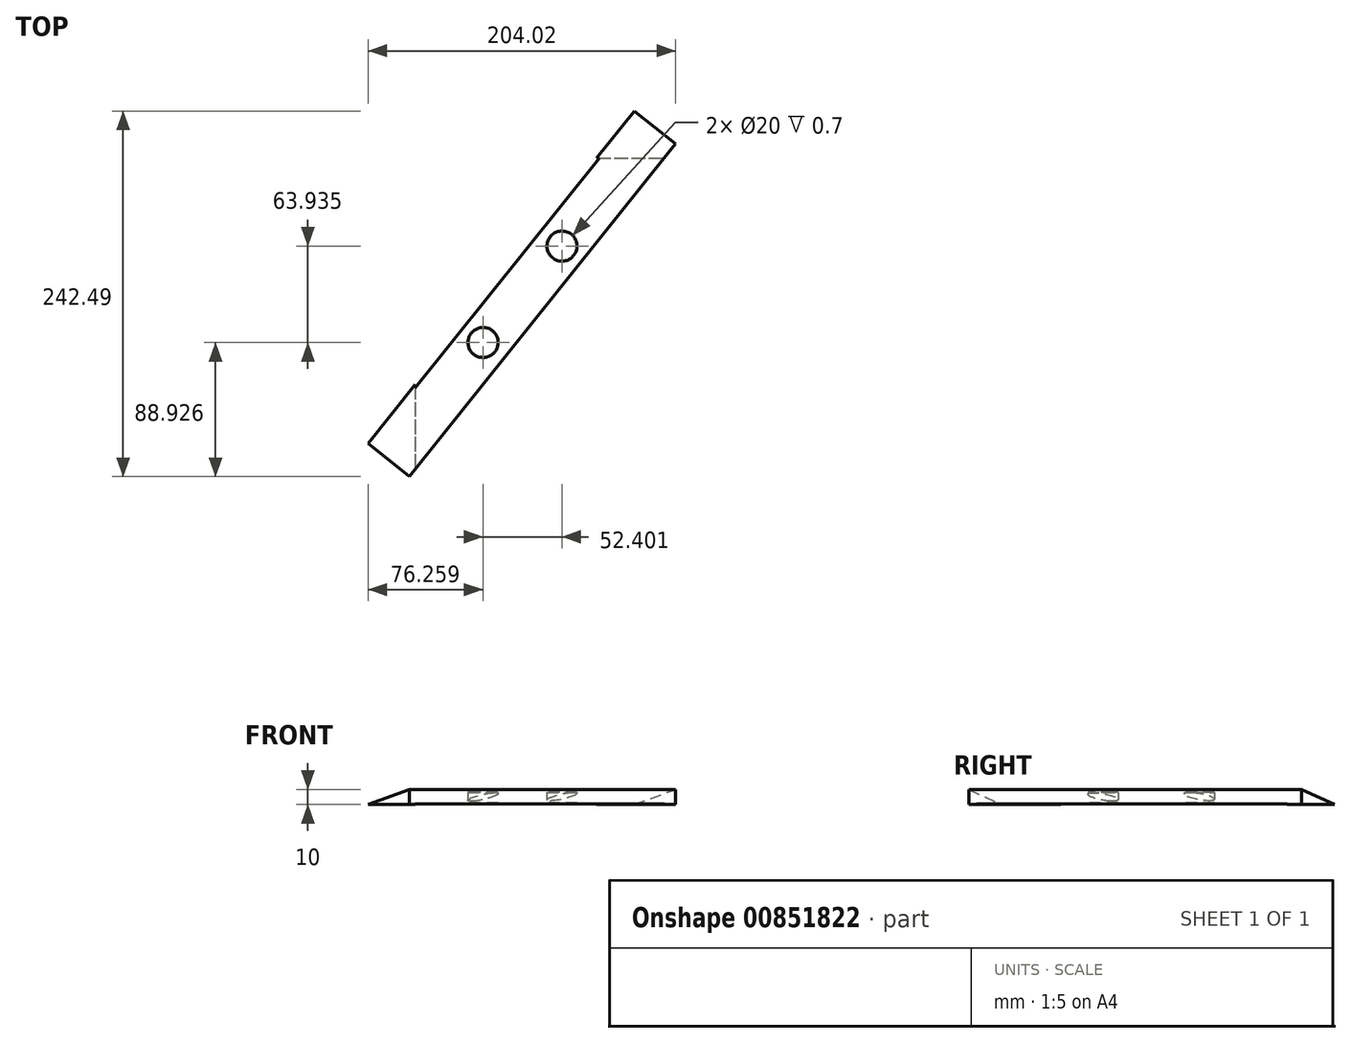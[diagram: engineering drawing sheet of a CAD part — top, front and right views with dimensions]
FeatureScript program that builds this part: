
annotation { "Feature Type Name" : "Feature", "Feature Type Description" : "" }
export const myFeature = defineFeature(function(context is Context, id is Id, definition is map)
    precondition{}
    {
        {
            var Q0;
            Q0=qCreatedBy(makeId("Top.planeOp"),FACE);
            var sketch = newSketch(context, id + "F0", { "sketchPlane" : qUnion([Q0])});
            skLineSegment(sketch, "E0.bottom", {"start": v(-264.2, 336.11) * mm, "end": v(-24.2, 336.11) * mm});
            skLineSegment(sketch, "E0.top", {"start": v(-264.2, 16.11) * mm, "end": v(-24.2, 16.11) * mm});
            skLineSegment(sketch, "E0.left", {"start": v(-264.2, 336.11) * mm, "end": v(-264.2, 16.11) * mm});
            skLineSegment(sketch, "E0.right", {"start": v(-24.2, 336.11) * mm, "end": v(-24.2, 16.11) * mm});
            skLineSegment(sketch, "E1", {"start": v(-264.2, 185.75) * mm, "end": v(-108.6, 61.11) * mm});
            skLineSegment(sketch, "E2", {"start": v(-264.2, 185.75) * mm, "end": v(-143.77, 336.11) * mm});
            skLineSegment(sketch, "E3", {"start": v(-108.6, 61.11) * mm, "end": v(-24.2, 166.48) * mm});
            skLineSegment(sketch, "E4", {"start": v(-24.2, 166.48) * mm, "end": v(-179.81, 291.11) * mm});
            skLineSegment(sketch, "E5.bottom", {"start": v(-268.15, 124.84) * mm, "end": v(-91.45, 345.45) * mm});
            skLineSegment(sketch, "E5.top", {"start": v(-295.47, 146.72) * mm, "end": v(-118.77, 367.33) * mm});
            skLineSegment(sketch, "E5.left", {"start": v(-295.47, 146.72) * mm, "end": v(-268.15, 124.84) * mm});
            skLineSegment(sketch, "E5.right", {"start": v(-118.77, 367.33) * mm, "end": v(-91.45, 345.45) * mm});
            skLineSegment(sketch, "E6.bottom", {"start": v(-257.84, 237.67) * mm, "end": v(-285.66, 202.93) * mm});
            skLineSegment(sketch, "E6.top", {"start": v(-13.84, 42.24) * mm, "end": v(-41.66, 7.5) * mm});
            skLineSegment(sketch, "E6.left", {"start": v(-285.66, 202.93) * mm, "end": v(-41.66, 7.5) * mm});
            skLineSegment(sketch, "E6.right", {"start": v(-257.84, 237.67) * mm, "end": v(-13.84, 42.24) * mm});
            skSolve(sketch);
        }
        {
            var Q0;
            {var subQ5=sQuery(id+"F0.wireOp",EDGE,"E5.right");Q0=makeQuery(id+"F0.imprint","IMPRINT",FACE,{"disambiguationData":[TD([[makeQuery(id+"F0.imprint","IMPRINT",EDGE,{"derivedFrom":subQ5}),-1.0]])]});}
            var Q1;
            {var subQ3=sQuery(id+"F0.wireOp",EDGE,"E2");var subQ5=sQuery(id+"F0.wireOp",EDGE,"E4");var subQ6=makeQuery(id+"F0.imprint","INTERSECT",VERTEX,{"derivedFrom":[subQ3,subQ5]});Q1=makeQuery(id+"F0.imprint","IMPRINT",FACE,{"disambiguationData":[TD([[makeQuery(id+"F0.imprint","IMPRINT",EDGE,{"disambiguationData":[TD([[subQ6,1.0]])],"derivedFrom":subQ5}),-1.0]])]});}
            var Q2;
            {var subQ0=sQuery(id+"F0.wireOp",EDGE,"E6.right");var subQ1=sQuery(id+"F0.wireOp",EDGE,"E2");var subQ2=makeQuery(id+"F0.imprint","INTERSECT",VERTEX,{"derivedFrom":[subQ1,subQ0]});Q2=makeQuery(id+"F0.imprint","IMPRINT",FACE,{"disambiguationData":[TD([[makeQuery(id+"F0.imprint","IMPRINT",EDGE,{"disambiguationData":[TD([[subQ2,-1.0]])],"derivedFrom":subQ1}),-1.0]])]});}
            var Q3;
            {var subQ5=sQuery(id+"F0.wireOp",EDGE,"E5.left");Q3=makeQuery(id+"F0.imprint","IMPRINT",FACE,{"disambiguationData":[TD([[makeQuery(id+"F0.imprint","IMPRINT",EDGE,{"derivedFrom":subQ5}),1.0]])]});}
            var Q4;
            {var subQ0=sQuery(id+"F0.wireOp",EDGE,"E5.bottom");var subQ1=sQuery(id+"F0.wireOp",EDGE,"E0.left");var subQ2=makeQuery(id+"F0.imprint","INTERSECT",VERTEX,{"derivedFrom":[subQ1,subQ0]});Q4=makeQuery(id+"F0.imprint","IMPRINT",FACE,{"disambiguationData":[TD([[makeQuery(id+"F0.imprint","IMPRINT",EDGE,{"disambiguationData":[TD([[subQ2,-1.0]])],"derivedFrom":subQ0}),1.0]])]});}
            var Q5;
            {var subQ1=sQuery(id+"F0.wireOp",EDGE,"E1");var subQ3=sQuery(id+"F0.wireOp",EDGE,"E5.bottom");var subQ4=makeQuery(id+"F0.imprint","INTERSECT",VERTEX,{"derivedFrom":[subQ1,subQ3]});Q5=makeQuery(id+"F0.imprint","IMPRINT",FACE,{"disambiguationData":[TD([[makeQuery(id+"F0.imprint","IMPRINT",EDGE,{"disambiguationData":[TD([[subQ4,-1.0]])],"derivedFrom":subQ3}),1.0]])]});}
            extrude(context, id + "F1", {"entities" : qUnion([Q0, Q1, Q2, Q3, Q4, Q5]), "depth" : 10 * mm, "offsetDistance" : 25 * mm});
        }
        {
            var Q0;
            {var subQ3=sQuery(id+"F0.wireOp",EDGE,"E2");var subQ5=sQuery(id+"F0.wireOp",EDGE,"E4");var subQ6=makeQuery(id+"F0.imprint","INTERSECT",VERTEX,{"derivedFrom":[subQ3,subQ5]});Q0=makeQuery(id+"F0.imprint","IMPRINT",FACE,{"disambiguationData":[TD([[makeQuery(id+"F0.imprint","IMPRINT",EDGE,{"disambiguationData":[TD([[subQ6,1.0]])],"derivedFrom":subQ5}),-1.0]])]});}
            var Q1;
            {var subQ0=sQuery(id+"F0.wireOp",EDGE,"E6.right");var subQ1=sQuery(id+"F0.wireOp",EDGE,"E2");var subQ2=makeQuery(id+"F0.imprint","INTERSECT",VERTEX,{"derivedFrom":[subQ1,subQ0]});Q1=makeQuery(id+"F0.imprint","IMPRINT",FACE,{"disambiguationData":[TD([[makeQuery(id+"F0.imprint","IMPRINT",EDGE,{"disambiguationData":[TD([[subQ2,-1.0]])],"derivedFrom":subQ1}),-1.0]])]});}
            var Q2;
            {var subQ0=sQuery(id+"F0.wireOp",EDGE,"E5.bottom");var subQ1=sQuery(id+"F0.wireOp",EDGE,"E0.left");var subQ2=makeQuery(id+"F0.imprint","INTERSECT",VERTEX,{"derivedFrom":[subQ1,subQ0]});Q2=makeQuery(id+"F0.imprint","IMPRINT",FACE,{"disambiguationData":[TD([[makeQuery(id+"F0.imprint","IMPRINT",EDGE,{"disambiguationData":[TD([[subQ2,-1.0]])],"derivedFrom":subQ0}),1.0]])]});}
            var Q3;
            Q3=makeQuery(id+"F1.opExtrude","CAP_FACE",FACE,{"disambiguationData":[OSD([sQuery(id+"F0.wireOp",EDGE,"E2"),sQuery(id+"F0.wireOp",EDGE,"E5.bottom"),sQuery(id+"F0.wireOp",EDGE,"E5.top"),sQuery(id+"F0.wireOp",EDGE,"E5.left"),sQuery(id+"F0.wireOp",EDGE,"E5.right")])],"isStart":false});
            var Q4;
            {var subQ1=sQuery(id+"F0.wireOp",EDGE,"E1");var subQ3=sQuery(id+"F0.wireOp",EDGE,"E5.bottom");var subQ4=makeQuery(id+"F0.imprint","INTERSECT",VERTEX,{"derivedFrom":[subQ1,subQ3]});Q4=makeQuery(id+"F0.imprint","IMPRINT",FACE,{"disambiguationData":[TD([[makeQuery(id+"F0.imprint","IMPRINT",EDGE,{"disambiguationData":[TD([[subQ4,-1.0]])],"derivedFrom":subQ3}),1.0]])]});}
            extrude(context, id + "F2", {"entities" : qUnion([Q0, Q1, Q2, Q3, Q4]), "operationType" : NewBodyOperationType.REMOVE, "depth" : 0.4 * mm, "offsetDistance" : 25 * mm});
        }
        {
            var Q0;
            Q0=makeQuery(id+"F1.opExtrude","SWEPT_FACE",FACE,{"disambiguationData":[OSD([sQuery(id+"F0.wireOp",EDGE,"E5.left")])]});
            var sketch = newSketch(context, id + "F3", { "sketchPlane" : qUnion([Q0])});
            skLineSegment(sketch, "E7.bottom", {"start": v(-290.92, 22.55) * mm, "end": v(-287.34, 10) * mm});
            skLineSegment(sketch, "E7.top", {"start": v(-325.92, 12.55) * mm, "end": v(-322.34, 0) * mm});
            skLineSegment(sketch, "E7.left", {"start": v(-287.34, 10) * mm, "end": v(-322.34, 0) * mm});
            skLineSegment(sketch, "E7.right", {"start": v(-290.92, 22.55) * mm, "end": v(-325.92, 12.55) * mm});
            skSolve(sketch);
        }
        {
            var Q0;
            Q0=makeQuery(id+"F3.imprint","IMPRINT",FACE,{"disambiguationData":[TD([[makeQuery(id+"F3.imprint","IMPRINT",EDGE,{"derivedFrom":sQuery(id+"F3.wireOp",EDGE,"E7.left")}),-1.0]])]});
            var Q1;
            Q1=makeQuery(id+"F3.imprint","IMPRINT",FACE,{"disambiguationData":[TD([[makeQuery(id+"F3.imprint","IMPRINT",EDGE,{"derivedFrom":sQuery(id+"F3.wireOp",EDGE,"E7.bottom")}),-1.0]])]});
            extrude(context, id + "F4", {"entities" : qUnion([Q0, Q1]), "operationType" : NewBodyOperationType.REMOVE, "oppositeDirection" : true, "depth" : 319.7 * mm, "offsetDistance" : 25 * mm});
        }
        {
            var Q0;
            Q0=qCreatedBy(makeId("Top.planeOp"),FACE);
            var sketch = newSketch(context, id + "F5", { "sketchPlane" : qUnion([Q0])});
            skCircle(sketch, "E8", {"center": v(-219.21, 213.77) * mm, "radius": 10 * mm});
            skCircle(sketch, "E9", {"center": v(-166.81, 277.7) * mm, "radius": 10 * mm});
            skSolve(sketch);
        }
        {
            var Q0;
            Q0 = qSketchRegion(id + "F5", true);
            extrude(context, id + "F6", {"entities" : qUnion([Q0]), "operationType" : NewBodyOperationType.ADD, "depth" : 8.1 * mm, "offsetDistance" : 25 * mm});
        }
        {
            var Q0;
            Q0 = qSketchRegion(id + "F5", true);
            extrude(context, id + "F7", {"entities" : qUnion([Q0]), "operationType" : NewBodyOperationType.REMOVE, "depth" : 1.1 * mm, "offsetDistance" : 25 * mm});
        }
    });
